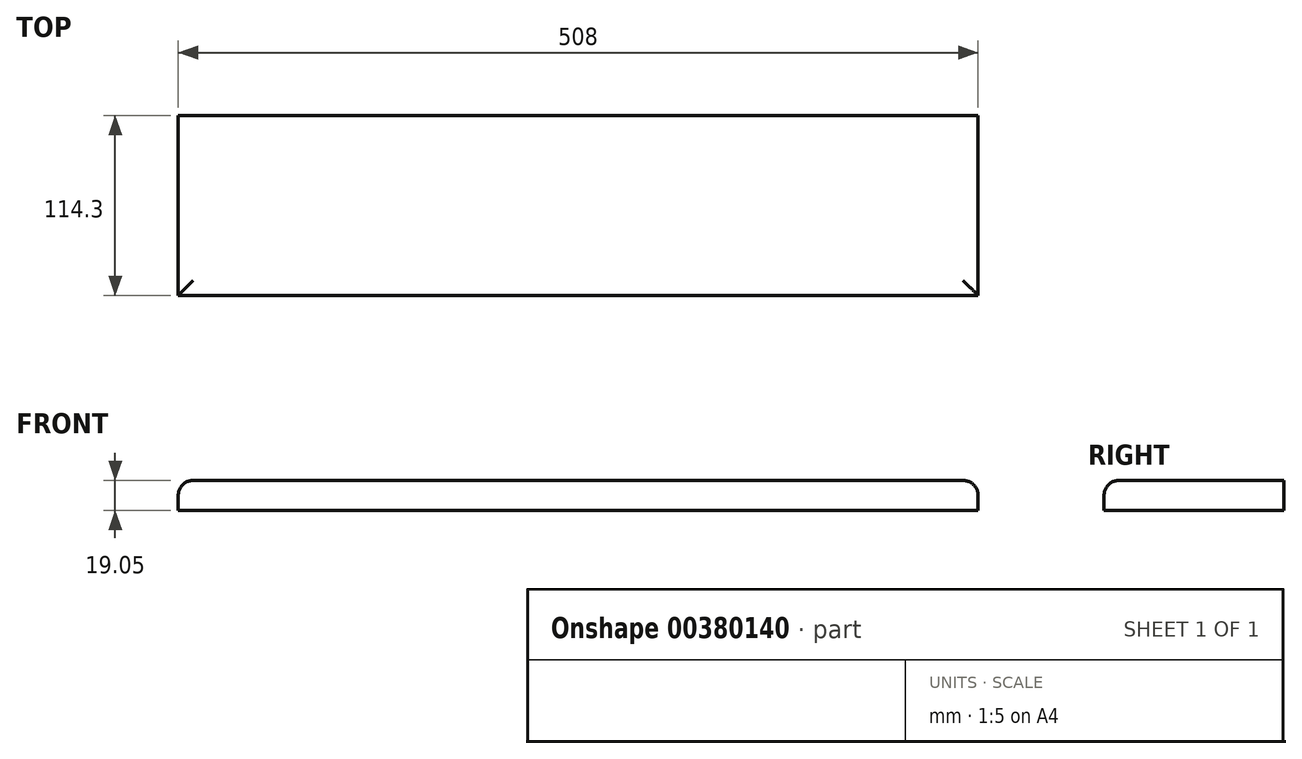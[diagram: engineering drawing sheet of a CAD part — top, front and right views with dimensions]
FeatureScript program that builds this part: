
annotation { "Feature Type Name" : "Feature", "Feature Type Description" : "" }
export const myFeature = defineFeature(function(context is Context, id is Id, definition is map)
    precondition{}
    {
        {
            var Q0;
            Q0=qCreatedBy(makeId("Top.planeOp"),FACE);
            var sketch = newSketch(context, id + "F0", { "sketchPlane" : qUnion([Q0])});
            skLineSegment(sketch, "E0.bottom", {"start": v(-254, 0) * mm, "end": v(254, 0) * mm});
            skLineSegment(sketch, "E0.top", {"start": v(-254, -114.3) * mm, "end": v(254, -114.3) * mm});
            skLineSegment(sketch, "E0.left", {"start": v(-254, 0) * mm, "end": v(-254, -114.3) * mm});
            skLineSegment(sketch, "E0.right", {"start": v(254, 0) * mm, "end": v(254, -114.3) * mm});
            skSolve(sketch);
        }
        {
            var Q0;
            Q0 = qSketchRegion(id + "F0", true);
            extrude(context, id + "F1", {"entities" : qUnion([Q0]), "depth" : 19.05 * mm});
        }
        {
            var Q0;
            Q0=makeQuery(id+"F1.opExtrude","CAP_EDGE",EDGE,{"disambiguationData":[OSD([sQuery(id+"F0.wireOp",EDGE,"E0.left")])],"isStart":false});
            var Q1;
            Q1=makeQuery(id+"F1.opExtrude","CAP_EDGE",EDGE,{"disambiguationData":[OSD([sQuery(id+"F0.wireOp",EDGE,"E0.top")])],"isStart":false});
            var Q2;
            Q2=makeQuery(id+"F1.opExtrude","CAP_EDGE",EDGE,{"disambiguationData":[OSD([sQuery(id+"F0.wireOp",EDGE,"E0.right")])],"isStart":false});
            fillet(context, id + "F2", {"entities" : qUnion([Q0, Q1, Q2]), "radius" : 9.52 * mm, "tangentPropagation" : true, "allowEdgeOverflow" : false});
        }
    });
